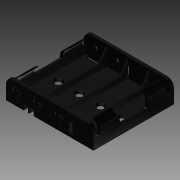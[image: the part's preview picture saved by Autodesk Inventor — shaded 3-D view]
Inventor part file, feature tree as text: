
AUTODESK INVENTOR PART (.ipt)
format: ipt  version: 2015 (Build 190159000, 159)  size: 522,752 bytes
history: native  units: mm
features: sketch x21, extrude x18, projected_geometry x9, fillet x4, mirror x3, hole x3, other x1, pattern_linear x1, chamfer x1
ambient origin geometry x8: Origin, YZ Plane, XZ Plane, XY Plane, X Axis, Y Axis, Z Axis, Center Point
bodies: Body1 (feature_tree)
feature tree (61):
  other  "솔리드1"
  extrude  "돌출1"  Depth=62.0mm
  extrude  "돌출2"  Depth=57.0mm
  fillet  "모깎기1"  Radius=1.5mm
  mirror  "대칭1"
  extrude  "돌출3"  Depth=15.0mm
  fillet  "모깎기2"  Radius=2.0mm
  mirror  "대칭2"
  extrude  "돌출4"  Depth=5.0mm
  fillet  "모깎기3"  Radius=14.0mm
  mirror  "대칭3"
  extrude  "돌출5"  Depth=8.5mm
  fillet  "모깎기4"  Radius=7.0mm
  extrude  "돌출6"  Depth=7.0mm
  extrude  "돌출7"  Depth=2.0mm TaperAngle=0.0deg
  extrude  "돌출8"  Depth=2.0mm
  extrude  "돌출9"  Depth=2.0mm
  extrude  "돌출10"  Depth=7.0mm
  extrude  "돌출11"  Depth=2.0mm TaperAngle=0.0deg
  extrude  "돌출12"  Depth=1.0mm
  extrude  "돌출13"  Depth=17.453293mm
  extrude  "돌출14"  Depth=19.0mm
  extrude  "돌출15"  Depth=17.453293mm
  extrude  "돌출16"  Depth=2.0mm TaperAngle=0.0deg
  extrude  "돌출17"  Depth=1.0mm
  extrude  "돌출18"  Depth=14.0mm
  hole  "구멍1"  [1 undecoded]
  hole  "구멍2"  [1 undecoded]
  hole  "구멍3"  [1 undecoded]
  pattern_linear  "직사각형 패턴1"  Spacing1=2.0mm  [1 undecoded]
  chamfer  "모따기1"  Distance=5.0mm
  sketch  "스케치1"
  sketch  "스케치2"
  projected_geometry  "투영된 루프1"
  sketch  "스케치3"
  sketch  "스케치4"
  sketch  "스케치5"
  sketch  "스케치6"
  projected_geometry  "투영된 루프2"
  sketch  "스케치7"
  projected_geometry  "투영된 루프3"
  sketch  "스케치8"
  sketch  "스케치9"
  sketch  "스케치10"
  sketch  "스케치11"
  sketch  "스케치12"
  sketch  "스케치13"
  sketch  "스케치14"
  sketch  "스케치15"
  sketch  "스케치16"
  sketch  "스케치17"
  projected_geometry  "투영된 루프4"
  sketch  "스케치18"
  projected_geometry  "투영된 루프5"
  projected_geometry  "투영된 루프6"
  sketch  "스케치19"
  projected_geometry  "투영된 루프7"
  projected_geometry  "투영된 루프8"
  projected_geometry  "투영된 루프9"
  sketch  "스케치20"
  sketch  "스케치21"
note: 4 required parameter values undecoded (feature->parameter linkage not recoverable at this tier; creation-order binding heuristic only, values carry confidence <= 0.55)
